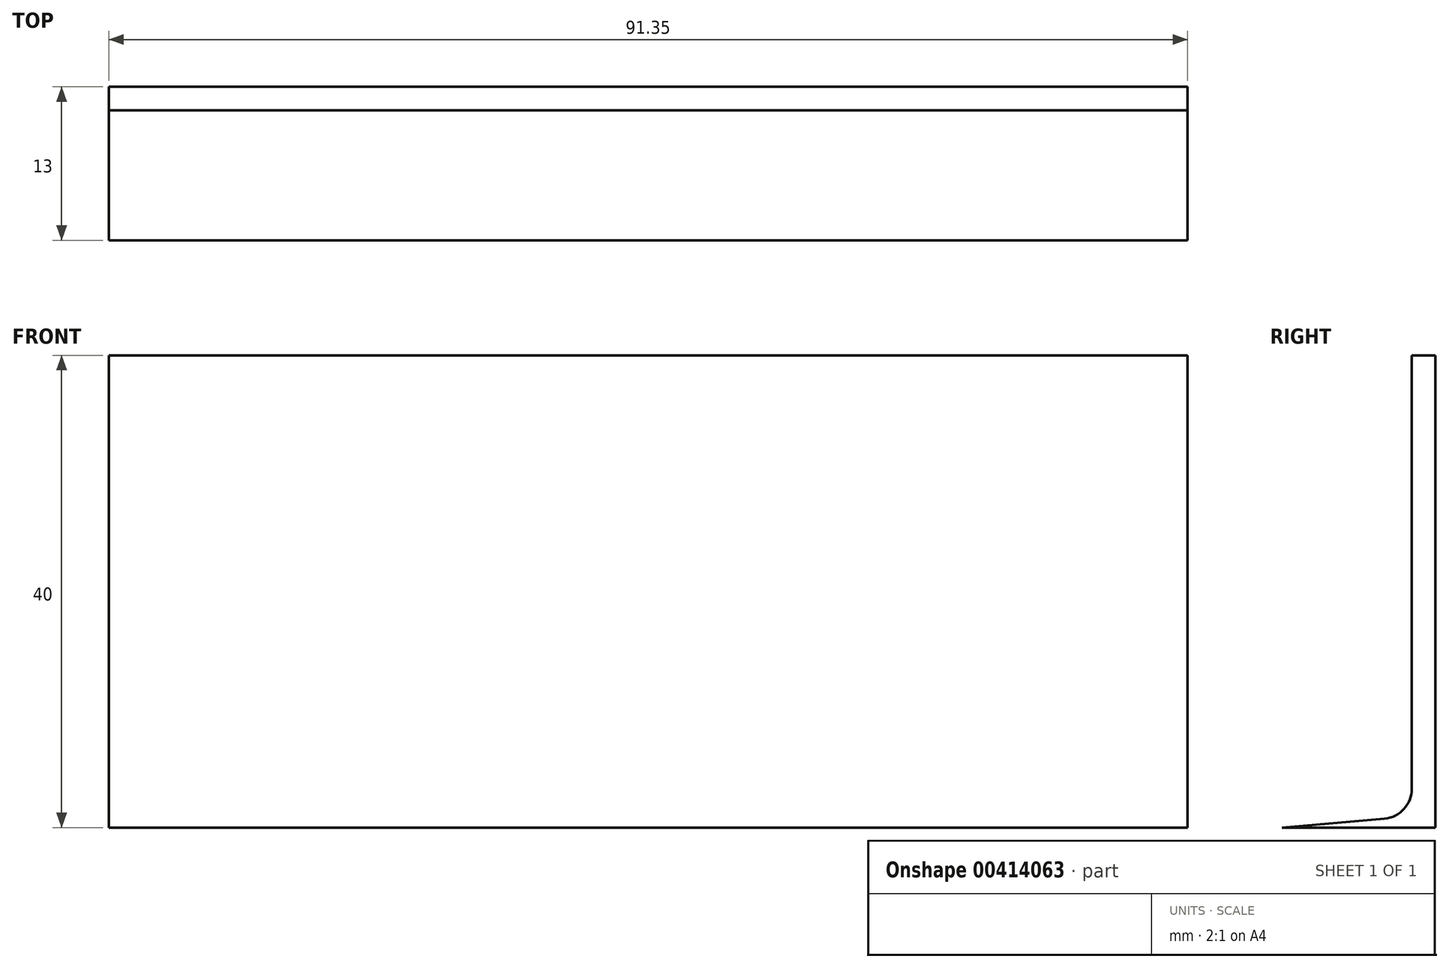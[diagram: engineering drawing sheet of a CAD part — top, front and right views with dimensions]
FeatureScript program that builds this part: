
annotation { "Feature Type Name" : "Feature", "Feature Type Description" : "" }
export const myFeature = defineFeature(function(context is Context, id is Id, definition is map)
    precondition{}
    {
        {
            var Q0;
            Q0=qCreatedBy(makeId("Front.planeOp"),FACE);
            var sketch = newSketch(context, id + "F0", { "sketchPlane" : qUnion([Q0])});
            skLineSegment(sketch, "E0.bottom", {"start": v(0, 0) * mm, "end": v(91.35, 0) * mm});
            skLineSegment(sketch, "E0.top", {"start": v(0, 40) * mm, "end": v(91.35, 40) * mm});
            skLineSegment(sketch, "E0.left", {"start": v(0, 0) * mm, "end": v(0, 40) * mm});
            skLineSegment(sketch, "E0.right", {"start": v(91.35, 0) * mm, "end": v(91.35, 40) * mm});
            skSolve(sketch);
        }
        {
            var Q0;
            Q0=makeQuery(id+"F0.imprint","IMPRINT",FACE,{"disambiguationData":[TD([[makeQuery(id+"F0.imprint","IMPRINT",EDGE,{"derivedFrom":sQuery(id+"F0.wireOp",EDGE,"E0.bottom")}),1.0]])]});
            extrude(context, id + "F1", {"entities" : qUnion([Q0]), "depth" : 13 * mm});
        }
        {
            var Q0;
            Q0=makeQuery(id+"F1.opExtrude","SWEPT_FACE",FACE,{"disambiguationData":[OSD([sQuery(id+"F0.wireOp",EDGE,"E0.right")])]});
            var sketch = newSketch(context, id + "F2", { "sketchPlane" : qUnion([Q0])});
            skLineSegment(sketch, "E1", {"start": v(-13, 0) * mm, "end": v(-2, 0.96) * mm});
            skLineSegment(sketch, "E2.bottom", {"start": v(0, 0) * mm, "end": v(-2, 0) * mm});
            skLineSegment(sketch, "E2.top", {"start": v(0, 40) * mm, "end": v(-2, 40) * mm});
            skLineSegment(sketch, "E2.left", {"start": v(0, 0) * mm, "end": v(0, 40) * mm});
            skLineSegment(sketch, "E2.right", {"start": v(-2, 0.96) * mm, "end": v(-2, 40) * mm});
            skSolve(sketch);
        }
        {
            var Q0;
            Q0=makeQuery(id+"F2.imprint","IMPRINT",FACE,{"disambiguationData":[TD([[makeQuery(id+"F2.imprint","IMPRINT",EDGE,{"derivedFrom":sQuery(id+"F2.wireOp",EDGE,"E1")}),1.0]])]});
            extrude(context, id + "F3", {"entities" : qUnion([Q0]), "operationType" : NewBodyOperationType.REMOVE, "oppositeDirection" : true, "depth" : 127 * mm});
        }
        {
            var Q0;
            Q0=makeQuery(id+"F3.boolean.opBoolean","COPY",EDGE,{"derivedFrom":makeQuery(id+"F3.opExtrude","SWEPT_EDGE",EDGE,{"disambiguationData":[OSD([sQuery(id+"F2.wireOp",EDGE,"E1"),sQuery(id+"F2.wireOp",EDGE,"E2.right")])]})});
            fillet(context, id + "F4", {"entities" : qUnion([Q0]), "radius" : 2.54 * mm, "tangentPropagation" : true, "allowEdgeOverflow" : false});
        }
    });
